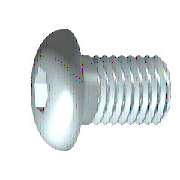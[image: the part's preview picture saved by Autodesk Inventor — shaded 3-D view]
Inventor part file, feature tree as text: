
AUTODESK INVENTOR PART (.ipt)
format: ipt  version: 2015 (Build 190159000, 159)  size: 194,048 bytes
history: native  units: mm (DEFAULTED — no unit token found)
features: sketch x2, other x1, extrude x1, plane x1
ambient origin geometry x7: Origin, YZ Plane, XY Plane, X Axis, Y Axis, Z Axis, Center Point
bodies: Body1 (feature_tree)
feature tree (5):
  other  "Bryła"
  extrude  "Szczelina"  Depth=18.0mm
  plane  "Work Plane1"
  sketch  "Szkic1"
  sketch  "Szkic2"
